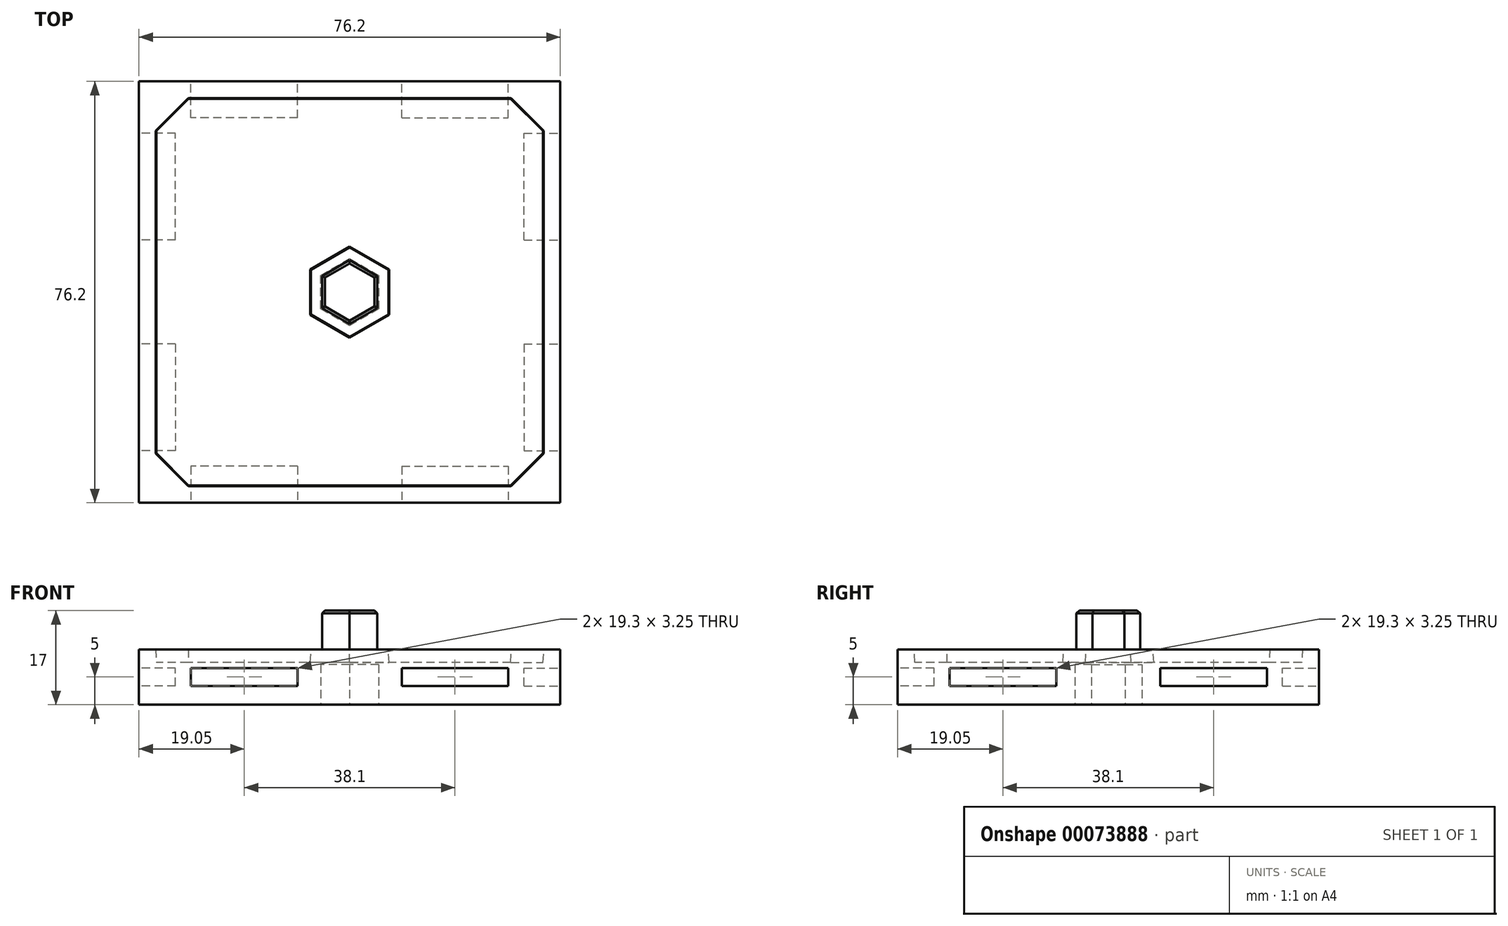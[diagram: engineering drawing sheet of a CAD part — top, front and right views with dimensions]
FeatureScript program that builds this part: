
annotation { "Feature Type Name" : "Feature", "Feature Type Description" : "" }
export const myFeature = defineFeature(function(context is Context, id is Id, definition is map)
    precondition{}
    {
        {
            var Q0;
            Q0=qCreatedBy(makeId("Top.planeOp"),FACE);
            var sketch = newSketch(context, id + "F0", { "sketchPlane" : qUnion([Q0])});
            skLineSegment(sketch, "E0.rect.bottom", {"start": v(38.1, -38.1) * mm, "end": v(-38.1, -38.1) * mm});
            skLineSegment(sketch, "E0.rect.top", {"start": v(38.1, 38.1) * mm, "end": v(-38.1, 38.1) * mm});
            skLineSegment(sketch, "E0.rect.left", {"start": v(38.1, -38.1) * mm, "end": v(38.1, 38.1) * mm});
            skLineSegment(sketch, "E0.rect.right", {"start": v(-38.1, -38.1) * mm, "end": v(-38.1, 38.1) * mm});
            skPoint(sketch, "E0.rect.middle", {"position": v(0, 0) * mm});
            skSolve(sketch);
        }
        {
            var Q0;
            Q0=makeQuery(id+"F0.imprint","IMPRINT",FACE,{"disambiguationData":[TD([[makeQuery(id+"F0.imprint","IMPRINT",EDGE,{"derivedFrom":sQuery(id+"F0.wireOp",EDGE,"E0.rect.bottom")}),-1.0]])]});
            extrude(context, id + "F1", {"entities" : qUnion([Q0]), "depth" : 10 * mm});
        }
        {
            var Q0;
            Q0=makeQuery(id+"F1.opExtrude","CAP_FACE",FACE,{"disambiguationData":[OSD([sQuery(id+"F0.wireOp",EDGE,"E0.rect.bottom"),sQuery(id+"F0.wireOp",EDGE,"E0.rect.top"),sQuery(id+"F0.wireOp",EDGE,"E0.rect.left"),sQuery(id+"F0.wireOp",EDGE,"E0.rect.right")])],"isStart":false});
            var sketch = newSketch(context, id + "F2", { "sketchPlane" : qUnion([Q0])});
            skCircle(sketch, "E1.cCircle", {"center": v(0, 0) * mm, "radius": 5 * mm, "construction": true});
            skLineSegment(sketch, "E1.0", {"start": v(5, 2.89) * mm, "end": v(5, -2.89) * mm});
            skLineSegment(sketch, "E1.1", {"start": v(5, -2.89) * mm, "end": v(0, -5.77) * mm});
            skLineSegment(sketch, "E1.2", {"start": v(0, -5.77) * mm, "end": v(-5, -2.89) * mm});
            skLineSegment(sketch, "E1.3", {"start": v(-5, -2.89) * mm, "end": v(-5, 2.89) * mm});
            skLineSegment(sketch, "E1.4", {"start": v(-5, 2.89) * mm, "end": v(0, 5.77) * mm});
            skLineSegment(sketch, "E1.5", {"start": v(0, 5.77) * mm, "end": v(5, 2.89) * mm});
            skPoint(sketch, "E1.0.midPoint", {"position": v(5, 0) * mm});
            skSolve(sketch);
        }
        {
            var Q0;
            Q0=makeQuery(id+"F2.imprint","IMPRINT",FACE,{"disambiguationData":[TD([[makeQuery(id+"F2.imprint","IMPRINT",EDGE,{"derivedFrom":sQuery(id+"F2.wireOp",EDGE,"E1.0")}),-1.0]])]});
            extrude(context, id + "F3", {"entities" : qUnion([Q0]), "operationType" : NewBodyOperationType.ADD, "depth" : 7 * mm});
        }
        {
            var Q0;
            Q0=makeQuery(id+"F1.opExtrude","CAP_FACE",FACE,{"disambiguationData":[OSD([sQuery(id+"F0.wireOp",EDGE,"E0.rect.bottom"),sQuery(id+"F0.wireOp",EDGE,"E0.rect.top"),sQuery(id+"F0.wireOp",EDGE,"E0.rect.left"),sQuery(id+"F0.wireOp",EDGE,"E0.rect.right")])],"isStart":true});
            var sketch = newSketch(context, id + "F4", { "sketchPlane" : qUnion([Q0])});
            skCircle(sketch, "E2.0", {"center": v(0, 0) * mm, "radius": 5 * mm, "construction": true});
            skLineSegment(sketch, "E2.1", {"start": v(5, -2.89) * mm, "end": v(5, 2.89) * mm, "construction": true});
            skLineSegment(sketch, "E2.2", {"start": v(5, 2.89) * mm, "end": v(0, 5.77) * mm, "construction": true});
            skLineSegment(sketch, "E2.3", {"start": v(0, 5.77) * mm, "end": v(-5, 2.89) * mm, "construction": true});
            skLineSegment(sketch, "E2.4", {"start": v(-5, 2.89) * mm, "end": v(-5, -2.89) * mm, "construction": true});
            skLineSegment(sketch, "E2.5", {"start": v(-5, -2.89) * mm, "end": v(0, -5.77) * mm, "construction": true});
            skLineSegment(sketch, "E2.6", {"start": v(0, -5.77) * mm, "end": v(5, -2.89) * mm, "construction": true});
            skPoint(sketch, "E2.7", {"position": v(5, 0) * mm});
            skLineSegment(sketch, "E3.0", {"start": v(5.25, 3.03) * mm, "end": v(0, 6.06) * mm});
            skLineSegment(sketch, "E3.1", {"start": v(-5.25, 3.03) * mm, "end": v(-5.25, -3.03) * mm});
            skLineSegment(sketch, "E3.2", {"start": v(-5.25, -3.03) * mm, "end": v(0, -6.06) * mm});
            skLineSegment(sketch, "E3.3", {"start": v(0, 6.06) * mm, "end": v(-5.25, 3.03) * mm});
            skLineSegment(sketch, "E3.4", {"start": v(0, -6.06) * mm, "end": v(5.25, -3.03) * mm});
            skLineSegment(sketch, "E3.5", {"start": v(5.25, -3.03) * mm, "end": v(5.25, 3.03) * mm});
            skSolve(sketch);
        }
        {
            var Q0;
            Q0=qSketchRegion(id+"F4",true);
            extrude(context, id + "F5", {"entities" : qUnion([Q0]), "operationType" : NewBodyOperationType.REMOVE, "oppositeDirection" : true, "depth" : 7.25 * mm});
        }
        {
            var Q0;
            Q0=makeQuery(id+"F1.opExtrude","SWEPT_FACE",FACE,{"disambiguationData":[OSD([sQuery(id+"F0.wireOp",EDGE,"E0.rect.bottom")])]});
            var sketch = newSketch(context, id + "F6", { "sketchPlane" : qUnion([Q0])});
            skLineSegment(sketch, "E4", {"start": v(0, 0) * mm, "end": v(0, 5) * mm, "construction": true});
            skLineSegment(sketch, "E5", {"start": v(-6.35, 5) * mm, "end": v(6.35, 5) * mm, "construction": true});
            skLineSegment(sketch, "E6.rect.bottom", {"start": v(-6.35, 0) * mm, "end": v(-31.75, 0) * mm, "construction": true});
            skLineSegment(sketch, "E6.rect.top", {"start": v(-6.35, 10) * mm, "end": v(-31.75, 10) * mm, "construction": true});
            skLineSegment(sketch, "E6.rect.left", {"start": v(-6.35, 0) * mm, "end": v(-6.35, 10) * mm, "construction": true});
            skLineSegment(sketch, "E6.rect.right", {"start": v(-31.75, 0) * mm, "end": v(-31.75, 10) * mm, "construction": true});
            skPoint(sketch, "E6.rect.middle", {"position": v(-19.05, 5) * mm});
            skLineSegment(sketch, "E7", {"start": v(-44.45, 5) * mm, "end": v(-31.75, 5) * mm, "construction": true});
            skPoint(sketch, "E8", {"position": v(-38.1, 5) * mm});
            skLineSegment(sketch, "E9.rect.bottom", {"start": v(-9.4, 3.37) * mm, "end": v(-28.7, 3.37) * mm});
            skLineSegment(sketch, "E9.rect.top", {"start": v(-9.4, 6.62) * mm, "end": v(-28.7, 6.63) * mm});
            skLineSegment(sketch, "E9.rect.left", {"start": v(-9.4, 3.37) * mm, "end": v(-9.4, 6.62) * mm});
            skLineSegment(sketch, "E9.rect.right", {"start": v(-28.7, 3.37) * mm, "end": v(-28.7, 6.62) * mm});
            skPoint(sketch, "E10.MirrorP", {"position": v(19.05, 5) * mm});
            skLineSegment(sketch, "E11.MirrorCS", {"start": v(28.7, 3.37) * mm, "end": v(28.7, 6.62) * mm});
            skLineSegment(sketch, "E12.MirrorCS", {"start": v(9.4, 3.37) * mm, "end": v(9.4, 6.62) * mm});
            skLineSegment(sketch, "E13.MirrorCS", {"start": v(9.4, 3.37) * mm, "end": v(28.7, 3.37) * mm});
            skLineSegment(sketch, "E14.MirrorCS", {"start": v(9.4, 6.62) * mm, "end": v(28.7, 6.63) * mm});
            skSolve(sketch);
        }
        {
            var Q0;
            Q0=qCreatedBy(makeId("Front.planeOp"),FACE);
            var sketch = newSketch(context, id + "F7", { "sketchPlane" : qUnion([Q0])});
            skLineSegment(sketch, "E15", {"start": v(0, 40.14) * mm, "end": v(0, 0) * mm, "construction": true});
            skSolve(sketch);
        }
        {
            var Q0;
            Q0=qSketchRegion(id+"F6",true);
            extrude(context, id + "F8", {"entities" : qUnion([Q0]), "oppositeDirection" : true, "depth" : 6.35 * mm + .25 * mm});
        }
        {
            var Q0;
            Q0=makeQuery(id+"F8.opExtrude","SWEPT_BODY",BODY,{"disambiguationData":[OSD([sQuery(id+"F6.wireOp",EDGE,"E11.MirrorCS"),sQuery(id+"F6.wireOp",EDGE,"E12.MirrorCS"),sQuery(id+"F6.wireOp",EDGE,"E13.MirrorCS"),sQuery(id+"F6.wireOp",EDGE,"E14.MirrorCS")])]});
            var Q1;
            Q1=makeQuery(id+"F8.opExtrude","SWEPT_BODY",BODY,{"disambiguationData":[OSD([sQuery(id+"F6.wireOp",EDGE,"E9.rect.bottom"),sQuery(id+"F6.wireOp",EDGE,"E9.rect.top"),sQuery(id+"F6.wireOp",EDGE,"E9.rect.left"),sQuery(id+"F6.wireOp",EDGE,"E9.rect.right")])]});
            var Q2;
            Q2=sQuery(id+"F7.wireOp",EDGE,"E15");
            circularPattern(context, id + "F9", {"entities" : qUnion([Q0, Q1]), "axis" : qUnion([Q2]), "angle" : 90 * degree, "instanceCount" : 4});
        }
        {
            var Q0;
            Q0=makeQuery(id+"F9.opPattern","COPY",BODY,{"derivedFrom":makeQuery(id+"F8.opExtrude","SWEPT_BODY",BODY,{"disambiguationData":[OSD([sQuery(id+"F6.wireOp",EDGE,"E11.MirrorCS"),sQuery(id+"F6.wireOp",EDGE,"E12.MirrorCS"),sQuery(id+"F6.wireOp",EDGE,"E13.MirrorCS"),sQuery(id+"F6.wireOp",EDGE,"E14.MirrorCS")])]}),"instanceName":"3"});
            var Q1;
            Q1=makeQuery(id+"F9.opPattern","COPY",BODY,{"derivedFrom":makeQuery(id+"F8.opExtrude","SWEPT_BODY",BODY,{"disambiguationData":[OSD([sQuery(id+"F6.wireOp",EDGE,"E9.rect.bottom"),sQuery(id+"F6.wireOp",EDGE,"E9.rect.top"),sQuery(id+"F6.wireOp",EDGE,"E9.rect.left"),sQuery(id+"F6.wireOp",EDGE,"E9.rect.right")])]}),"instanceName":"3"});
            var Q2;
            Q2=makeQuery(id+"F9.opPattern","COPY",BODY,{"derivedFrom":makeQuery(id+"F8.opExtrude","SWEPT_BODY",BODY,{"disambiguationData":[OSD([sQuery(id+"F6.wireOp",EDGE,"E11.MirrorCS"),sQuery(id+"F6.wireOp",EDGE,"E12.MirrorCS"),sQuery(id+"F6.wireOp",EDGE,"E13.MirrorCS"),sQuery(id+"F6.wireOp",EDGE,"E14.MirrorCS")])]}),"instanceName":"2"});
            var Q3;
            Q3=makeQuery(id+"F9.opPattern","COPY",BODY,{"derivedFrom":makeQuery(id+"F8.opExtrude","SWEPT_BODY",BODY,{"disambiguationData":[OSD([sQuery(id+"F6.wireOp",EDGE,"E9.rect.bottom"),sQuery(id+"F6.wireOp",EDGE,"E9.rect.top"),sQuery(id+"F6.wireOp",EDGE,"E9.rect.left"),sQuery(id+"F6.wireOp",EDGE,"E9.rect.right")])]}),"instanceName":"2"});
            var Q4;
            Q4=makeQuery(id+"F9.opPattern","COPY",BODY,{"derivedFrom":makeQuery(id+"F8.opExtrude","SWEPT_BODY",BODY,{"disambiguationData":[OSD([sQuery(id+"F6.wireOp",EDGE,"E11.MirrorCS"),sQuery(id+"F6.wireOp",EDGE,"E12.MirrorCS"),sQuery(id+"F6.wireOp",EDGE,"E13.MirrorCS"),sQuery(id+"F6.wireOp",EDGE,"E14.MirrorCS")])]}),"instanceName":"1"});
            var Q5;
            Q5=makeQuery(id+"F9.opPattern","COPY",BODY,{"derivedFrom":makeQuery(id+"F8.opExtrude","SWEPT_BODY",BODY,{"disambiguationData":[OSD([sQuery(id+"F6.wireOp",EDGE,"E9.rect.bottom"),sQuery(id+"F6.wireOp",EDGE,"E9.rect.top"),sQuery(id+"F6.wireOp",EDGE,"E9.rect.left"),sQuery(id+"F6.wireOp",EDGE,"E9.rect.right")])]}),"instanceName":"1"});
            var Q6;
            Q6=makeQuery(id+"F8.opExtrude","SWEPT_BODY",BODY,{"disambiguationData":[OSD([sQuery(id+"F6.wireOp",EDGE,"E11.MirrorCS"),sQuery(id+"F6.wireOp",EDGE,"E12.MirrorCS"),sQuery(id+"F6.wireOp",EDGE,"E13.MirrorCS"),sQuery(id+"F6.wireOp",EDGE,"E14.MirrorCS")])]});
            var Q7;
            Q7=makeQuery(id+"F8.opExtrude","SWEPT_BODY",BODY,{"disambiguationData":[OSD([sQuery(id+"F6.wireOp",EDGE,"E9.rect.bottom"),sQuery(id+"F6.wireOp",EDGE,"E9.rect.top"),sQuery(id+"F6.wireOp",EDGE,"E9.rect.left"),sQuery(id+"F6.wireOp",EDGE,"E9.rect.right")])]});
            var Q8;
            Q8=makeQuery(id+"F1.opExtrude","SWEPT_BODY",BODY,{"disambiguationData":[OSD([sQuery(id+"F0.wireOp",EDGE,"E0.rect.bottom"),sQuery(id+"F0.wireOp",EDGE,"E0.rect.top"),sQuery(id+"F0.wireOp",EDGE,"E0.rect.left"),sQuery(id+"F0.wireOp",EDGE,"E0.rect.right")])]});
            booleanBodies(context, id + "F10", {"operationType" : BooleanOperationType.SUBTRACTION, "tools" : qUnion([Q0, Q1, Q2, Q3, Q4, Q5, Q6, Q7]), "targets" : qUnion([Q8])});
        }
        {
            var Q0;
            Q0=makeQuery(id+"F3.opExtrude","CAP_FACE",FACE,{"disambiguationData":[OSD([sQuery(id+"F2.wireOp",EDGE,"E1.0"),sQuery(id+"F2.wireOp",EDGE,"E1.1"),sQuery(id+"F2.wireOp",EDGE,"E1.2"),sQuery(id+"F2.wireOp",EDGE,"E1.3"),sQuery(id+"F2.wireOp",EDGE,"E1.4"),sQuery(id+"F2.wireOp",EDGE,"E1.5")])],"isStart":false});
            var Q1;
            Q1=makeQuery(id+"F5.boolean.opBoolean","COPY",EDGE,{"derivedFrom":makeQuery(id+"F5.opExtrude","CAP_EDGE",EDGE,{"disambiguationData":[OSD([sQuery(id+"F4.wireOp",EDGE,"E3.4")])],"isStart":true})});
            var Q2;
            Q2=makeQuery(id+"F5.boolean.opBoolean","COPY",EDGE,{"derivedFrom":makeQuery(id+"F5.opExtrude","CAP_EDGE",EDGE,{"disambiguationData":[OSD([sQuery(id+"F4.wireOp",EDGE,"E3.5")])],"isStart":true})});
            var Q3;
            Q3=makeQuery(id+"F5.boolean.opBoolean","COPY",EDGE,{"derivedFrom":makeQuery(id+"F5.opExtrude","CAP_EDGE",EDGE,{"disambiguationData":[OSD([sQuery(id+"F4.wireOp",EDGE,"E3.0")])],"isStart":true})});
            var Q4;
            Q4=makeQuery(id+"F5.boolean.opBoolean","COPY",EDGE,{"derivedFrom":makeQuery(id+"F5.opExtrude","CAP_EDGE",EDGE,{"disambiguationData":[OSD([sQuery(id+"F4.wireOp",EDGE,"E3.3")])],"isStart":true})});
            var Q5;
            Q5=makeQuery(id+"F5.boolean.opBoolean","COPY",EDGE,{"derivedFrom":makeQuery(id+"F5.opExtrude","CAP_EDGE",EDGE,{"disambiguationData":[OSD([sQuery(id+"F4.wireOp",EDGE,"E3.1")])],"isStart":true})});
            var Q6;
            Q6=makeQuery(id+"F5.boolean.opBoolean","COPY",EDGE,{"derivedFrom":makeQuery(id+"F5.opExtrude","CAP_EDGE",EDGE,{"disambiguationData":[OSD([sQuery(id+"F4.wireOp",EDGE,"E3.2")])],"isStart":true})});
            var Q7;
            Q7=makeQuery(id+"F10.opBoolean","COPY",EDGE,{"derivedFrom":makeQuery(id+"F9.opPattern","COPY",EDGE,{"derivedFrom":makeQuery(id+"F8.opExtrude","CAP_EDGE",EDGE,{"disambiguationData":[OSD([sQuery(id+"F6.wireOp",EDGE,"E9.rect.top")])],"isStart":true}),"instanceName":"3"})});
            var Q8;
            Q8=makeQuery(id+"F10.opBoolean","COPY",EDGE,{"derivedFrom":makeQuery(id+"F9.opPattern","COPY",EDGE,{"derivedFrom":makeQuery(id+"F8.opExtrude","CAP_EDGE",EDGE,{"disambiguationData":[OSD([sQuery(id+"F6.wireOp",EDGE,"E9.rect.left")])],"isStart":true}),"instanceName":"3"})});
            var Q9;
            Q9=makeQuery(id+"F10.opBoolean","COPY",EDGE,{"derivedFrom":makeQuery(id+"F9.opPattern","COPY",EDGE,{"derivedFrom":makeQuery(id+"F8.opExtrude","CAP_EDGE",EDGE,{"disambiguationData":[OSD([sQuery(id+"F6.wireOp",EDGE,"E9.rect.bottom")])],"isStart":true}),"instanceName":"3"})});
            var Q10;
            Q10=makeQuery(id+"F10.opBoolean","COPY",EDGE,{"derivedFrom":makeQuery(id+"F9.opPattern","COPY",EDGE,{"derivedFrom":makeQuery(id+"F8.opExtrude","CAP_EDGE",EDGE,{"disambiguationData":[OSD([sQuery(id+"F6.wireOp",EDGE,"E9.rect.right")])],"isStart":true}),"instanceName":"3"})});
            var Q11;
            Q11=makeQuery(id+"F10.opBoolean","COPY",EDGE,{"derivedFrom":makeQuery(id+"F9.opPattern","COPY",EDGE,{"derivedFrom":makeQuery(id+"F8.opExtrude","CAP_EDGE",EDGE,{"disambiguationData":[OSD([sQuery(id+"F6.wireOp",EDGE,"E13.MirrorCS")])],"isStart":true}),"instanceName":"3"})});
            var Q12;
            Q12=makeQuery(id+"F10.opBoolean","COPY",EDGE,{"derivedFrom":makeQuery(id+"F9.opPattern","COPY",EDGE,{"derivedFrom":makeQuery(id+"F8.opExtrude","CAP_EDGE",EDGE,{"disambiguationData":[OSD([sQuery(id+"F6.wireOp",EDGE,"E12.MirrorCS")])],"isStart":true}),"instanceName":"3"})});
            var Q13;
            Q13=makeQuery(id+"F10.opBoolean","COPY",EDGE,{"derivedFrom":makeQuery(id+"F9.opPattern","COPY",EDGE,{"derivedFrom":makeQuery(id+"F8.opExtrude","CAP_EDGE",EDGE,{"disambiguationData":[OSD([sQuery(id+"F6.wireOp",EDGE,"E11.MirrorCS")])],"isStart":true}),"instanceName":"3"})});
            var Q14;
            Q14=makeQuery(id+"F10.opBoolean","COPY",EDGE,{"derivedFrom":makeQuery(id+"F9.opPattern","COPY",EDGE,{"derivedFrom":makeQuery(id+"F8.opExtrude","CAP_EDGE",EDGE,{"disambiguationData":[OSD([sQuery(id+"F6.wireOp",EDGE,"E14.MirrorCS")])],"isStart":true}),"instanceName":"3"})});
            var Q15;
            Q15=makeQuery(id+"F10.opBoolean","COPY",EDGE,{"derivedFrom":makeQuery(id+"F9.opPattern","COPY",EDGE,{"derivedFrom":makeQuery(id+"F8.opExtrude","CAP_EDGE",EDGE,{"disambiguationData":[OSD([sQuery(id+"F6.wireOp",EDGE,"E9.rect.top")])],"isStart":true}),"instanceName":"2"})});
            var Q16;
            Q16=makeQuery(id+"F10.opBoolean","COPY",EDGE,{"derivedFrom":makeQuery(id+"F9.opPattern","COPY",EDGE,{"derivedFrom":makeQuery(id+"F8.opExtrude","CAP_EDGE",EDGE,{"disambiguationData":[OSD([sQuery(id+"F6.wireOp",EDGE,"E9.rect.right")])],"isStart":true}),"instanceName":"2"})});
            var Q17;
            Q17=makeQuery(id+"F10.opBoolean","COPY",EDGE,{"derivedFrom":makeQuery(id+"F9.opPattern","COPY",EDGE,{"derivedFrom":makeQuery(id+"F8.opExtrude","CAP_EDGE",EDGE,{"disambiguationData":[OSD([sQuery(id+"F6.wireOp",EDGE,"E9.rect.left")])],"isStart":true}),"instanceName":"2"})});
            var Q18;
            Q18=makeQuery(id+"F10.opBoolean","COPY",EDGE,{"derivedFrom":makeQuery(id+"F9.opPattern","COPY",EDGE,{"derivedFrom":makeQuery(id+"F8.opExtrude","CAP_EDGE",EDGE,{"disambiguationData":[OSD([sQuery(id+"F6.wireOp",EDGE,"E9.rect.bottom")])],"isStart":true}),"instanceName":"2"})});
            var Q19;
            Q19=makeQuery(id+"F10.opBoolean","COPY",EDGE,{"derivedFrom":makeQuery(id+"F8.opExtrude","CAP_EDGE",EDGE,{"disambiguationData":[OSD([sQuery(id+"F6.wireOp",EDGE,"E11.MirrorCS")])],"isStart":true})});
            var Q20;
            Q20=makeQuery(id+"F10.opBoolean","COPY",EDGE,{"derivedFrom":makeQuery(id+"F8.opExtrude","CAP_EDGE",EDGE,{"disambiguationData":[OSD([sQuery(id+"F6.wireOp",EDGE,"E14.MirrorCS")])],"isStart":true})});
            var Q21;
            Q21=makeQuery(id+"F10.opBoolean","COPY",EDGE,{"derivedFrom":makeQuery(id+"F8.opExtrude","CAP_EDGE",EDGE,{"disambiguationData":[OSD([sQuery(id+"F6.wireOp",EDGE,"E12.MirrorCS")])],"isStart":true})});
            var Q22;
            Q22=makeQuery(id+"F10.opBoolean","COPY",EDGE,{"derivedFrom":makeQuery(id+"F8.opExtrude","CAP_EDGE",EDGE,{"disambiguationData":[OSD([sQuery(id+"F6.wireOp",EDGE,"E13.MirrorCS")])],"isStart":true})});
            var Q23;
            Q23=makeQuery(id+"F10.opBoolean","COPY",EDGE,{"derivedFrom":makeQuery(id+"F8.opExtrude","CAP_EDGE",EDGE,{"disambiguationData":[OSD([sQuery(id+"F6.wireOp",EDGE,"E9.rect.left")])],"isStart":true})});
            var Q24;
            Q24=makeQuery(id+"F10.opBoolean","COPY",EDGE,{"derivedFrom":makeQuery(id+"F8.opExtrude","CAP_EDGE",EDGE,{"disambiguationData":[OSD([sQuery(id+"F6.wireOp",EDGE,"E9.rect.top")])],"isStart":true})});
            var Q25;
            Q25=makeQuery(id+"F10.opBoolean","COPY",EDGE,{"derivedFrom":makeQuery(id+"F8.opExtrude","CAP_EDGE",EDGE,{"disambiguationData":[OSD([sQuery(id+"F6.wireOp",EDGE,"E9.rect.bottom")])],"isStart":true})});
            var Q26;
            Q26=makeQuery(id+"F10.opBoolean","COPY",EDGE,{"derivedFrom":makeQuery(id+"F8.opExtrude","CAP_EDGE",EDGE,{"disambiguationData":[OSD([sQuery(id+"F6.wireOp",EDGE,"E9.rect.right")])],"isStart":true})});
            var Q27;
            Q27=makeQuery(id+"F10.opBoolean","COPY",EDGE,{"derivedFrom":makeQuery(id+"F9.opPattern","COPY",EDGE,{"derivedFrom":makeQuery(id+"F8.opExtrude","CAP_EDGE",EDGE,{"disambiguationData":[OSD([sQuery(id+"F6.wireOp",EDGE,"E11.MirrorCS")])],"isStart":true}),"instanceName":"1"})});
            var Q28;
            Q28=makeQuery(id+"F10.opBoolean","COPY",EDGE,{"derivedFrom":makeQuery(id+"F9.opPattern","COPY",EDGE,{"derivedFrom":makeQuery(id+"F8.opExtrude","CAP_EDGE",EDGE,{"disambiguationData":[OSD([sQuery(id+"F6.wireOp",EDGE,"E14.MirrorCS")])],"isStart":true}),"instanceName":"1"})});
            var Q29;
            Q29=makeQuery(id+"F10.opBoolean","COPY",EDGE,{"derivedFrom":makeQuery(id+"F9.opPattern","COPY",EDGE,{"derivedFrom":makeQuery(id+"F8.opExtrude","CAP_EDGE",EDGE,{"disambiguationData":[OSD([sQuery(id+"F6.wireOp",EDGE,"E12.MirrorCS")])],"isStart":true}),"instanceName":"1"})});
            var Q30;
            Q30=makeQuery(id+"F10.opBoolean","COPY",EDGE,{"derivedFrom":makeQuery(id+"F9.opPattern","COPY",EDGE,{"derivedFrom":makeQuery(id+"F8.opExtrude","CAP_EDGE",EDGE,{"disambiguationData":[OSD([sQuery(id+"F6.wireOp",EDGE,"E13.MirrorCS")])],"isStart":true}),"instanceName":"1"})});
            var Q31;
            Q31=makeQuery(id+"F10.opBoolean","COPY",EDGE,{"derivedFrom":makeQuery(id+"F9.opPattern","COPY",EDGE,{"derivedFrom":makeQuery(id+"F8.opExtrude","CAP_EDGE",EDGE,{"disambiguationData":[OSD([sQuery(id+"F6.wireOp",EDGE,"E9.rect.left")])],"isStart":true}),"instanceName":"1"})});
            var Q32;
            Q32=makeQuery(id+"F10.opBoolean","COPY",EDGE,{"derivedFrom":makeQuery(id+"F9.opPattern","COPY",EDGE,{"derivedFrom":makeQuery(id+"F8.opExtrude","CAP_EDGE",EDGE,{"disambiguationData":[OSD([sQuery(id+"F6.wireOp",EDGE,"E9.rect.top")])],"isStart":true}),"instanceName":"1"})});
            var Q33;
            Q33=makeQuery(id+"F10.opBoolean","COPY",EDGE,{"derivedFrom":makeQuery(id+"F9.opPattern","COPY",EDGE,{"derivedFrom":makeQuery(id+"F8.opExtrude","CAP_EDGE",EDGE,{"disambiguationData":[OSD([sQuery(id+"F6.wireOp",EDGE,"E9.rect.right")])],"isStart":true}),"instanceName":"1"})});
            var Q34;
            Q34=makeQuery(id+"F10.opBoolean","COPY",EDGE,{"derivedFrom":makeQuery(id+"F9.opPattern","COPY",EDGE,{"derivedFrom":makeQuery(id+"F8.opExtrude","CAP_EDGE",EDGE,{"disambiguationData":[OSD([sQuery(id+"F6.wireOp",EDGE,"E9.rect.bottom")])],"isStart":true}),"instanceName":"1"})});
            var Q35;
            Q35=makeQuery(id+"F10.opBoolean","COPY",EDGE,{"derivedFrom":makeQuery(id+"F9.opPattern","COPY",EDGE,{"derivedFrom":makeQuery(id+"F8.opExtrude","CAP_EDGE",EDGE,{"disambiguationData":[OSD([sQuery(id+"F6.wireOp",EDGE,"E14.MirrorCS")])],"isStart":true}),"instanceName":"2"})});
            var Q36;
            Q36=makeQuery(id+"F10.opBoolean","COPY",EDGE,{"derivedFrom":makeQuery(id+"F9.opPattern","COPY",EDGE,{"derivedFrom":makeQuery(id+"F8.opExtrude","CAP_EDGE",EDGE,{"disambiguationData":[OSD([sQuery(id+"F6.wireOp",EDGE,"E11.MirrorCS")])],"isStart":true}),"instanceName":"2"})});
            var Q37;
            Q37=makeQuery(id+"F10.opBoolean","COPY",EDGE,{"derivedFrom":makeQuery(id+"F9.opPattern","COPY",EDGE,{"derivedFrom":makeQuery(id+"F8.opExtrude","CAP_EDGE",EDGE,{"disambiguationData":[OSD([sQuery(id+"F6.wireOp",EDGE,"E12.MirrorCS")])],"isStart":true}),"instanceName":"2"})});
            var Q38;
            Q38=makeQuery(id+"F10.opBoolean","COPY",EDGE,{"derivedFrom":makeQuery(id+"F9.opPattern","COPY",EDGE,{"derivedFrom":makeQuery(id+"F8.opExtrude","CAP_EDGE",EDGE,{"disambiguationData":[OSD([sQuery(id+"F6.wireOp",EDGE,"E13.MirrorCS")])],"isStart":true}),"instanceName":"2"})});
            chamfer(context, id + "F11", {"entities" : qUnion([Q0, Q1, Q2, Q3, Q4, Q5, Q6, Q7, Q8, Q9, Q10, Q11, Q12, Q13, Q14, Q15, Q16, Q17, Q18, Q19, Q20, Q21, Q22, Q23, Q24, Q25, Q26, Q27, Q28, Q29, Q30, Q31, Q32, Q33, Q34, Q35, Q36, Q37, Q38]), "width" : .5 * mm, "tangentPropagation" : true});
        }
        {
            var Q0;
            Q0=qCreatedBy(makeId("Right.planeOp"),FACE);
            var sketch = newSketch(context, id + "F12", { "sketchPlane" : qUnion([Q0])});
            skLineSegment(sketch, "E16", {"start": v(0, 17) * mm, "end": v(0, 7) * mm, "construction": true});
            skSolve(sketch);
        }
        {
            var Q0;
            Q0=makeQuery(id+"F1.opExtrude","SWEPT_FACE",FACE,{"disambiguationData":[OSD([sQuery(id+"F0.wireOp",EDGE,"E0.rect.bottom")])]});
            var sketch = newSketch(context, id + "F13", { "sketchPlane" : qUnion([Q0])});
            skLineSegment(sketch, "E17.bottom", {"start": v(8.9, 2.87) * mm, "end": v(29.2, 2.87) * mm});
            skLineSegment(sketch, "E17.top", {"start": v(8.9, 7.12) * mm, "end": v(29.2, 7.12) * mm});
            skLineSegment(sketch, "E17.left", {"start": v(8.9, 2.87) * mm, "end": v(8.9, 7.12) * mm});
            skLineSegment(sketch, "E17.right", {"start": v(29.2, 2.87) * mm, "end": v(29.2, 7.12) * mm});
            skPoint(sketch, "E17.middle", {"position": v(19.05, 5) * mm});
            skPoint(sketch, "E17.middle.positionSnap0", {"position": v(19.05, 2.87) * mm});
            skPoint(sketch, "E17.middle.positionSnap1", {"position": v(8.9, 5) * mm});
            skPoint(sketch, "E17.centerSnap0", {"position": v(19.05, 2.87) * mm});
            skPoint(sketch, "E17.centerSnap1", {"position": v(8.9, 5) * mm});
            skLineSegment(sketch, "E18.bottom", {"start": v(-8.9, 2.87) * mm, "end": v(-29.2, 2.87) * mm});
            skLineSegment(sketch, "E18.top", {"start": v(-8.9, 7.12) * mm, "end": v(-29.2, 7.12) * mm});
            skLineSegment(sketch, "E18.left", {"start": v(-8.9, 2.87) * mm, "end": v(-8.9, 7.12) * mm});
            skLineSegment(sketch, "E18.right", {"start": v(-29.2, 2.87) * mm, "end": v(-29.2, 7.12) * mm});
            skPoint(sketch, "E18.middle", {"position": v(-19.05, 5) * mm});
            skPoint(sketch, "E18.middle.positionSnap0", {"position": v(-8.9, 5) * mm});
            skPoint(sketch, "E18.middle.positionSnap1", {"position": v(-19.05, 2.87) * mm});
            skPoint(sketch, "E18.centerSnap0", {"position": v(-8.9, 5) * mm});
            skPoint(sketch, "E18.centerSnap1", {"position": v(-19.05, 2.87) * mm});
            skSolve(sketch);
        }
        {
            var Q0;
            Q0=makeQuery(id+"F1.opExtrude","SWEPT_FACE",FACE,{"disambiguationData":[OSD([sQuery(id+"F0.wireOp",EDGE,"E0.rect.left")])]});
            var sketch = newSketch(context, id + "F14", { "sketchPlane" : qUnion([Q0])});
            skLineSegment(sketch, "E19.bottom", {"start": v(-29.2, 7.13) * mm, "end": v(-8.9, 7.13) * mm});
            skLineSegment(sketch, "E19.top", {"start": v(-29.2, 2.87) * mm, "end": v(-8.9, 2.87) * mm});
            skLineSegment(sketch, "E19.left", {"start": v(-29.2, 7.13) * mm, "end": v(-29.2, 2.87) * mm});
            skLineSegment(sketch, "E19.right", {"start": v(-8.9, 7.13) * mm, "end": v(-8.9, 2.87) * mm});
            skPoint(sketch, "E19.middle", {"position": v(-19.05, 5) * mm});
            skLineSegment(sketch, "E20.bottom", {"start": v(8.9, 7.13) * mm, "end": v(29.2, 7.13) * mm});
            skLineSegment(sketch, "E20.top", {"start": v(8.9, 2.87) * mm, "end": v(29.2, 2.87) * mm});
            skLineSegment(sketch, "E20.left", {"start": v(8.9, 7.13) * mm, "end": v(8.9, 2.87) * mm});
            skLineSegment(sketch, "E20.right", {"start": v(29.2, 7.13) * mm, "end": v(29.2, 2.87) * mm});
            skPoint(sketch, "E20.middle", {"position": v(19.05, 5) * mm});
            skPoint(sketch, "E20.middle.positionSnap0", {"position": v(29.2, 5) * mm});
            skPoint(sketch, "E20.middle.positionSnap1", {"position": v(19.05, 7.13) * mm});
            skPoint(sketch, "E20.centerSnap0", {"position": v(29.2, 5) * mm});
            skPoint(sketch, "E20.centerSnap1", {"position": v(19.05, 7.13) * mm});
            skSolve(sketch);
        }
        {
            var Q0;
            Q0=makeQuery(id+"F1.opExtrude","SWEPT_FACE",FACE,{"disambiguationData":[OSD([sQuery(id+"F0.wireOp",EDGE,"E0.rect.top")])]});
            var sketch = newSketch(context, id + "F15", { "sketchPlane" : qUnion([Q0])});
            skLineSegment(sketch, "E21.bottom", {"start": v(-29.2, 2.88) * mm, "end": v(-8.9, 2.88) * mm});
            skLineSegment(sketch, "E21.top", {"start": v(-29.2, 7.13) * mm, "end": v(-8.9, 7.13) * mm});
            skLineSegment(sketch, "E21.left", {"start": v(-29.2, 2.88) * mm, "end": v(-29.2, 7.13) * mm});
            skLineSegment(sketch, "E21.right", {"start": v(-8.9, 2.88) * mm, "end": v(-8.9, 7.13) * mm});
            skPoint(sketch, "E21.middle", {"position": v(-19.05, 5) * mm});
            skPoint(sketch, "E21.middle.positionSnap0", {"position": v(-29.2, 5) * mm});
            skPoint(sketch, "E21.middle.positionSnap1", {"position": v(-19.05, 7.13) * mm});
            skPoint(sketch, "E21.centerSnap0", {"position": v(-29.2, 5) * mm});
            skPoint(sketch, "E21.centerSnap1", {"position": v(-19.05, 7.13) * mm});
            skLineSegment(sketch, "E22.bottom", {"start": v(8.9, 2.87) * mm, "end": v(29.2, 2.87) * mm});
            skLineSegment(sketch, "E22.top", {"start": v(8.9, 7.12) * mm, "end": v(29.2, 7.12) * mm});
            skLineSegment(sketch, "E22.left", {"start": v(8.9, 2.87) * mm, "end": v(8.9, 7.12) * mm});
            skLineSegment(sketch, "E22.right", {"start": v(29.2, 2.87) * mm, "end": v(29.2, 7.12) * mm});
            skPoint(sketch, "E22.middle", {"position": v(19.05, 5) * mm});
            skPoint(sketch, "E22.middle.positionSnap0", {"position": v(19.05, 7.12) * mm});
            skPoint(sketch, "E22.middle.positionSnap1", {"position": v(8.9, 5) * mm});
            skPoint(sketch, "E22.centerSnap0", {"position": v(19.05, 7.12) * mm});
            skPoint(sketch, "E22.centerSnap1", {"position": v(8.9, 5) * mm});
            skSolve(sketch);
        }
        {
            var Q0;
            Q0=makeQuery(id+"F1.opExtrude","SWEPT_FACE",FACE,{"disambiguationData":[OSD([sQuery(id+"F0.wireOp",EDGE,"E0.rect.right")])]});
            var sketch = newSketch(context, id + "F16", { "sketchPlane" : qUnion([Q0])});
            skLineSegment(sketch, "E23.bottom", {"start": v(-29.2, 7.12) * mm, "end": v(-8.9, 7.12) * mm});
            skLineSegment(sketch, "E23.top", {"start": v(-29.2, 2.87) * mm, "end": v(-8.9, 2.87) * mm});
            skLineSegment(sketch, "E23.left", {"start": v(-29.2, 7.12) * mm, "end": v(-29.2, 2.87) * mm});
            skLineSegment(sketch, "E23.right", {"start": v(-8.9, 7.12) * mm, "end": v(-8.9, 2.87) * mm});
            skPoint(sketch, "E23.middle", {"position": v(-19.05, 5) * mm});
            skPoint(sketch, "E23.middle.positionSnap0", {"position": v(-19.05, 7.12) * mm});
            skPoint(sketch, "E23.middle.positionSnap1", {"position": v(-29.2, 5) * mm});
            skPoint(sketch, "E23.centerSnap0", {"position": v(-19.05, 7.12) * mm});
            skPoint(sketch, "E23.centerSnap1", {"position": v(-29.2, 5) * mm});
            skLineSegment(sketch, "E24.bottom", {"start": v(8.9, 7.12) * mm, "end": v(29.2, 7.12) * mm});
            skLineSegment(sketch, "E24.top", {"start": v(8.9, 2.87) * mm, "end": v(29.2, 2.87) * mm});
            skLineSegment(sketch, "E24.left", {"start": v(8.9, 7.12) * mm, "end": v(8.9, 2.87) * mm});
            skLineSegment(sketch, "E24.right", {"start": v(29.2, 7.12) * mm, "end": v(29.2, 2.87) * mm});
            skPoint(sketch, "E24.middle", {"position": v(19.05, 5) * mm});
            skPoint(sketch, "E24.middle.positionSnap0", {"position": v(19.05, 7.12) * mm});
            skPoint(sketch, "E24.middle.positionSnap1", {"position": v(8.9, 5) * mm});
            skPoint(sketch, "E24.centerSnap0", {"position": v(19.05, 7.12) * mm});
            skPoint(sketch, "E24.centerSnap1", {"position": v(8.9, 5) * mm});
            skSolve(sketch);
        }
        {
            var Q0;
            Q0=makeQuery(id+"F1.opExtrude","CAP_FACE",FACE,{"disambiguationData":[OSD([sQuery(id+"F0.wireOp",EDGE,"E0.rect.bottom"),sQuery(id+"F0.wireOp",EDGE,"E0.rect.top"),sQuery(id+"F0.wireOp",EDGE,"E0.rect.left"),sQuery(id+"F0.wireOp",EDGE,"E0.rect.right")])],"isStart":false});
            var sketch = newSketch(context, id + "F17", { "sketchPlane" : qUnion([Q0])});
            skLineSegment(sketch, "E25", {"start": v(-29.2, 35.1) * mm, "end": v(-8.9, 35.1) * mm});
            skLineSegment(sketch, "E26", {"start": v(-8.9, 35.1) * mm, "end": v(-8.9, 14.8) * mm});
            skLineSegment(sketch, "E27", {"start": v(-14.8, 8.9) * mm, "end": v(-35.1, 8.9) * mm});
            skLineSegment(sketch, "E28", {"start": v(-35.1, 8.9) * mm, "end": v(-35.1, 29.2) * mm});
            skLineSegment(sketch, "E29", {"start": v(0, 0) * mm, "end": v(-32.15, 32.15) * mm, "construction": true});
            skLineSegment(sketch, "E30", {"start": v(-8.9, 35.1) * mm, "end": v(-8.9, 38.1) * mm, "construction": true});
            skLineSegment(sketch, "E31", {"start": v(-29.2, 35.1) * mm, "end": v(-29.2, 38.1) * mm, "construction": true});
            skLineSegment(sketch, "E32", {"start": v(-35.1, 29.2) * mm, "end": v(-38.1, 29.2) * mm, "construction": true});
            skLineSegment(sketch, "E33.bottom", {"start": v(-5.9, 14.8) * mm, "end": v(5.9, 14.8) * mm});
            skLineSegment(sketch, "E33.top", {"start": v(-5.9, 35.1) * mm, "end": v(5.9, 35.1) * mm});
            skLineSegment(sketch, "E33.left", {"start": v(-5.9, 14.8) * mm, "end": v(-5.9, 35.1) * mm});
            skLineSegment(sketch, "E33.right", {"start": v(5.9, 14.8) * mm, "end": v(5.9, 35.1) * mm});
            skPoint(sketch, "E33.middle", {"position": v(0, 24.95) * mm});
            skLineSegment(sketch, "E34.1.5", {"start": v(-14.8, 5.9) * mm, "end": v(-35.1, 5.9) * mm});
            skLineSegment(sketch, "E34.1.6", {"start": v(-14.8, -5.9) * mm, "end": v(-14.8, 5.9) * mm});
            skLineSegment(sketch, "E34.1.7", {"start": v(-35.1, -5.9) * mm, "end": v(-35.1, 5.9) * mm});
            skLineSegment(sketch, "E34.1.8", {"start": v(-14.8, -5.9) * mm, "end": v(-35.1, -5.9) * mm});
            skPoint(sketch, "E34.1.9", {"position": v(-24.95, 0) * mm});
            skLineSegment(sketch, "E34.2.5", {"start": v(-5.9, -14.8) * mm, "end": v(-5.9, -35.1) * mm});
            skLineSegment(sketch, "E34.2.6", {"start": v(5.9, -14.8) * mm, "end": v(-5.9, -14.8) * mm});
            skLineSegment(sketch, "E34.2.7", {"start": v(5.9, -35.1) * mm, "end": v(-5.9, -35.1) * mm});
            skLineSegment(sketch, "E34.2.8", {"start": v(5.9, -14.8) * mm, "end": v(5.9, -35.1) * mm});
            skPoint(sketch, "E34.2.9", {"position": v(0, -24.95) * mm});
            skLineSegment(sketch, "E34.3.5", {"start": v(14.8, -5.9) * mm, "end": v(35.1, -5.9) * mm});
            skLineSegment(sketch, "E34.3.6", {"start": v(14.8, 5.9) * mm, "end": v(14.8, -5.9) * mm});
            skLineSegment(sketch, "E34.3.7", {"start": v(35.1, 5.9) * mm, "end": v(35.1, -5.9) * mm});
            skLineSegment(sketch, "E34.3.8", {"start": v(14.8, 5.9) * mm, "end": v(35.1, 5.9) * mm});
            skPoint(sketch, "E34.3.9", {"position": v(24.95, 0) * mm});
            skPoint(sketch, "E34.center", {"position": v(0, 0) * mm});
            skLineSegment(sketch, "E35.0", {"start": v(-10.79, 12.91) * mm, "end": v(-31.09, 33.21) * mm});
            skLineSegment(sketch, "E36.0", {"start": v(-12.91, 10.79) * mm, "end": v(-33.21, 31.09) * mm});
            skLineSegment(sketch, "E37.trimOffspring", {"start": v(-31.09, 33.21) * mm, "end": v(-29.2, 35.1) * mm});
            skLineSegment(sketch, "E38.trimOffspring", {"start": v(-12.91, 10.79) * mm, "end": v(-14.8, 8.9) * mm});
            skLineSegment(sketch, "E39", {"start": v(-10.79, 12.91) * mm, "end": v(-8.9, 14.8) * mm});
            skLineSegment(sketch, "E40", {"start": v(-33.21, 31.09) * mm, "end": v(-35.1, 29.2) * mm});
            skLineSegment(sketch, "E41.1.0", {"start": v(-35.1, -29.2) * mm, "end": v(-38.1, -29.2) * mm, "construction": true});
            skLineSegment(sketch, "E41.1.1", {"start": v(-35.1, -29.2) * mm, "end": v(-35.1, -8.9) * mm});
            skLineSegment(sketch, "E41.1.2", {"start": v(-10.79, -12.91) * mm, "end": v(-31.09, -33.21) * mm});
            skLineSegment(sketch, "E41.1.3", {"start": v(-35.1, -8.9) * mm, "end": v(-14.8, -8.9) * mm});
            skLineSegment(sketch, "E41.1.4", {"start": v(-8.9, -14.8) * mm, "end": v(-8.9, -35.1) * mm});
            skLineSegment(sketch, "E41.1.5", {"start": v(-8.9, -35.1) * mm, "end": v(-29.2, -35.1) * mm});
            skLineSegment(sketch, "E41.1.6", {"start": v(-12.91, -10.79) * mm, "end": v(-33.21, -31.09) * mm});
            skLineSegment(sketch, "E41.1.7", {"start": v(-35.1, -8.9) * mm, "end": v(-38.1, -8.9) * mm, "construction": true});
            skLineSegment(sketch, "E41.1.8", {"start": v(-33.21, -31.09) * mm, "end": v(-35.1, -29.2) * mm});
            skLineSegment(sketch, "E41.1.9", {"start": v(-31.09, -33.21) * mm, "end": v(-29.2, -35.1) * mm});
            skLineSegment(sketch, "E41.1.10", {"start": v(-10.79, -12.91) * mm, "end": v(-8.9, -14.8) * mm});
            skLineSegment(sketch, "E41.1.11", {"start": v(-12.91, -10.79) * mm, "end": v(-14.8, -8.9) * mm});
            skLineSegment(sketch, "E41.1.12", {"start": v(-29.2, -35.1) * mm, "end": v(-29.2, -38.1) * mm, "construction": true});
            skLineSegment(sketch, "E41.2.0", {"start": v(29.2, -35.1) * mm, "end": v(29.2, -38.1) * mm, "construction": true});
            skLineSegment(sketch, "E41.2.1", {"start": v(29.2, -35.1) * mm, "end": v(8.9, -35.1) * mm});
            skLineSegment(sketch, "E41.2.2", {"start": v(12.91, -10.79) * mm, "end": v(33.21, -31.09) * mm});
            skLineSegment(sketch, "E41.2.3", {"start": v(8.9, -35.1) * mm, "end": v(8.9, -14.8) * mm});
            skLineSegment(sketch, "E41.2.4", {"start": v(14.8, -8.9) * mm, "end": v(35.1, -8.9) * mm});
            skLineSegment(sketch, "E41.2.5", {"start": v(35.1, -8.9) * mm, "end": v(35.1, -29.2) * mm});
            skLineSegment(sketch, "E41.2.6", {"start": v(10.79, -12.91) * mm, "end": v(31.09, -33.21) * mm});
            skLineSegment(sketch, "E41.2.7", {"start": v(8.9, -35.1) * mm, "end": v(8.9, -38.1) * mm, "construction": true});
            skLineSegment(sketch, "E41.2.8", {"start": v(31.09, -33.21) * mm, "end": v(29.2, -35.1) * mm});
            skLineSegment(sketch, "E41.2.9", {"start": v(33.21, -31.09) * mm, "end": v(35.1, -29.2) * mm});
            skLineSegment(sketch, "E41.2.10", {"start": v(12.91, -10.79) * mm, "end": v(14.8, -8.9) * mm});
            skLineSegment(sketch, "E41.2.11", {"start": v(10.79, -12.91) * mm, "end": v(8.9, -14.8) * mm});
            skLineSegment(sketch, "E41.2.12", {"start": v(35.1, -29.2) * mm, "end": v(38.1, -29.2) * mm, "construction": true});
            skLineSegment(sketch, "E41.3.0", {"start": v(35.1, 29.2) * mm, "end": v(38.1, 29.2) * mm, "construction": true});
            skLineSegment(sketch, "E41.3.1", {"start": v(35.1, 29.2) * mm, "end": v(35.1, 8.9) * mm});
            skLineSegment(sketch, "E41.3.2", {"start": v(10.79, 12.91) * mm, "end": v(31.09, 33.21) * mm});
            skLineSegment(sketch, "E41.3.3", {"start": v(35.1, 8.9) * mm, "end": v(14.8, 8.9) * mm});
            skLineSegment(sketch, "E41.3.4", {"start": v(8.9, 14.8) * mm, "end": v(8.9, 35.1) * mm});
            skLineSegment(sketch, "E41.3.5", {"start": v(8.9, 35.1) * mm, "end": v(29.2, 35.1) * mm});
            skLineSegment(sketch, "E41.3.6", {"start": v(12.91, 10.79) * mm, "end": v(33.21, 31.09) * mm});
            skLineSegment(sketch, "E41.3.7", {"start": v(35.1, 8.9) * mm, "end": v(38.1, 8.9) * mm, "construction": true});
            skLineSegment(sketch, "E41.3.8", {"start": v(33.21, 31.09) * mm, "end": v(35.1, 29.2) * mm});
            skLineSegment(sketch, "E41.3.9", {"start": v(31.09, 33.21) * mm, "end": v(29.2, 35.1) * mm});
            skLineSegment(sketch, "E41.3.10", {"start": v(10.79, 12.91) * mm, "end": v(8.9, 14.8) * mm});
            skLineSegment(sketch, "E41.3.11", {"start": v(12.91, 10.79) * mm, "end": v(14.8, 8.9) * mm});
            skLineSegment(sketch, "E41.3.12", {"start": v(29.2, 35.1) * mm, "end": v(29.2, 38.1) * mm, "construction": true});
            skSolve(sketch);
        }
        {
            var Q0;
            Q0=makeQuery(id+"F17.imprint","IMPRINT",FACE,{"disambiguationData":[TD([[makeQuery(id+"F17.imprint","IMPRINT",EDGE,{"derivedFrom":sQuery(id+"F17.wireOp",EDGE,"E27")}),-1.0]])]});
            var sketch = newSketch(context, id + "F18", { "sketchPlane" : qUnion([Q0])});
            skLineSegment(sketch, "E42", {"start": v(-35.1, 29.2) * mm, "end": v(-29.2, 35.1) * mm});
            skLineSegment(sketch, "E43", {"start": v(-29.2, 35.1) * mm, "end": v(29.2, 35.1) * mm});
            skLineSegment(sketch, "E44", {"start": v(29.2, 35.1) * mm, "end": v(35.1, 29.2) * mm});
            skLineSegment(sketch, "E45", {"start": v(35.1, 29.2) * mm, "end": v(35.1, -29.2) * mm});
            skLineSegment(sketch, "E46", {"start": v(35.1, -29.2) * mm, "end": v(29.2, -35.1) * mm});
            skLineSegment(sketch, "E47", {"start": v(29.2, -35.1) * mm, "end": v(-29.2, -35.1) * mm});
            skLineSegment(sketch, "E48", {"start": v(-29.2, -35.1) * mm, "end": v(-35.1, -29.2) * mm});
            skLineSegment(sketch, "E49", {"start": v(-35.1, -29.2) * mm, "end": v(-35.1, 29.2) * mm});
            skCircle(sketch, "E50.cCircle", {"center": v(0, 0) * mm, "radius": 7 * mm, "construction": true});
            skLineSegment(sketch, "E50.0", {"start": v(-7, -4.04) * mm, "end": v(-7, 4.04) * mm});
            skLineSegment(sketch, "E50.1", {"start": v(-7, 4.04) * mm, "end": v(0, 8.08) * mm});
            skLineSegment(sketch, "E50.2", {"start": v(0, 8.08) * mm, "end": v(7, 4.04) * mm});
            skLineSegment(sketch, "E50.3", {"start": v(7, 4.04) * mm, "end": v(7, -4.04) * mm});
            skLineSegment(sketch, "E50.4", {"start": v(7, -4.04) * mm, "end": v(0, -8.08) * mm});
            skLineSegment(sketch, "E50.5", {"start": v(0, -8.08) * mm, "end": v(-7, -4.04) * mm});
            skPoint(sketch, "E50.0.midPoint", {"position": v(-7, 0) * mm});
            skSolve(sketch);
        }
        {
            var Q0;
            Q0 = qSketchRegion(id + "F18", true);
            extrude(context, id + "F19", {"entities" : qUnion([Q0]), "operationType" : NewBodyOperationType.REMOVE, "oppositeDirection" : true, "depth" : 2.38 * mm, "hasDraft" : true, "draftAngle" : 3 * degree, "draftPullDirection" : true});
        }
    });
